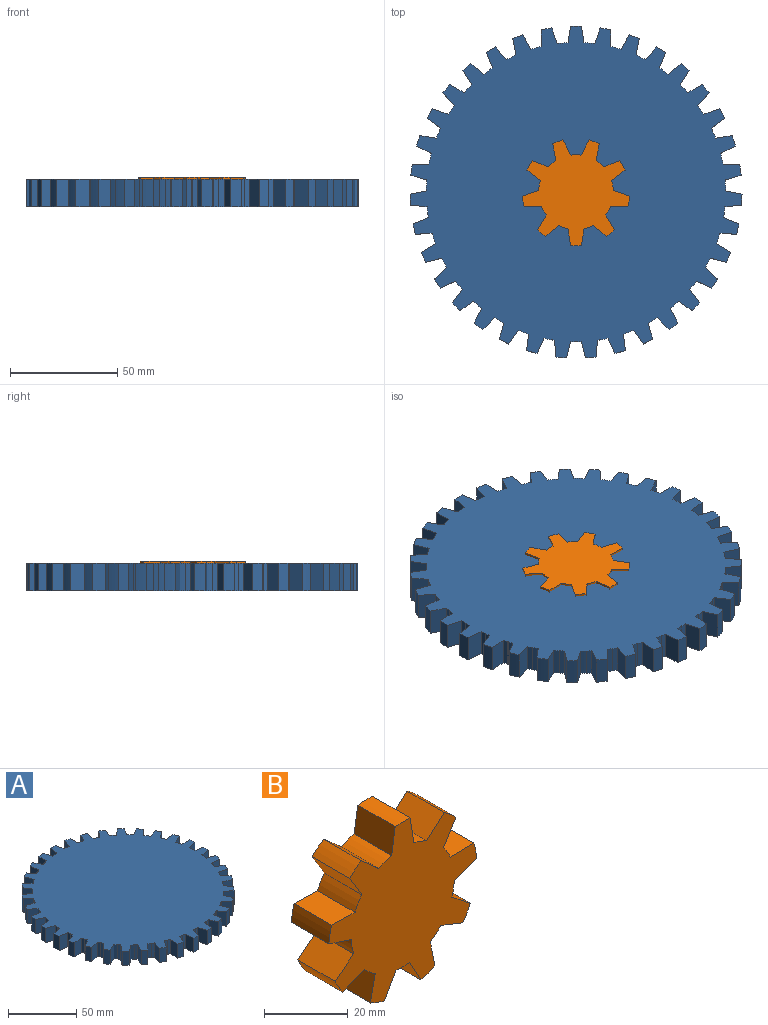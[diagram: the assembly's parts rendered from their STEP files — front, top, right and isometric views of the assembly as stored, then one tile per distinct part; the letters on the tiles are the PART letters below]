
ASSEMBLY  parts=2 mates=2
PART A: 212 faces, bbox 154.9x154.8x12.7 mm
  f0: plane 12.7x7.68mm, normal (0.99,0.15,0), area 98.7mm2, adj f1,f209,f210,f211
  f1: cylinder r=77.47mm len=12.7mm, axis (0,0,-1), area 64.5mm2, adj f0,f2,f210,f211
  f2: plane 12.7x7.68mm, normal (-0.99,0.15,0), area 98.7mm2, adj f1,f3,f210,f211
  f3: cylinder r=69.85mm len=12.7mm, axis (0,0,-1), area 32.2mm2, adj f2,f4,f210,f211
  f4: plane 12.7x0mm, normal (-0.09,1,0), area 0mm2, adj f3,f5,f210,f211
  f5: cylinder r=69.85mm len=12.7mm, axis (0,0,-1), area 32.2mm2, adj f4,f6,f210,f211
  f6: plane 12.7x7.34mm, normal (0.94,0.33,0), area 98.7mm2, adj f5,f7,f210,f211
  f7: cylinder r=77.47mm len=12.7mm, axis (0,0,-1), area 64.5mm2, adj f6,f8,f210,f211
  f8: plane 12.7x7.77mm, normal (-1,-0.03,0), area 98.7mm2, adj f7,f9,f210,f211
  f9: cylinder r=69.85mm len=12.7mm, axis (0,0,-1), area 32.2mm2, adj f8,f10,f210,f211
  f10: plane 12.7x0mm, normal (-0.27,0.96,0), area 0mm2, adj f9,f11,f210,f211
  f11: cylinder r=69.85mm len=12.7mm, axis (0,0,-1), area 32.2mm2, adj f10,f12,f210,f211
  f12: plane 12.7x6.77mm, normal (0.87,0.49,0), area 98.7mm2, adj f11,f13,f210,f211
  f13: cylinder r=77.47mm len=12.7mm, axis (0,0,-1), area 64.5mm2, adj f12,f14,f210,f211
  f14: plane 12.7x7.61mm, normal (-0.98,-0.2,0), area 98.7mm2, adj f13,f15,f210,f211
  f15: cylinder r=69.85mm len=12.7mm, axis (0,0,-1), area 32.2mm2, adj f14,f16,f210,f211
  f16: plane 12.7x0mm, normal (-0.43,0.9,0), area 0mm2, adj f15,f17,f210,f211
  f17: cylinder r=69.85mm len=12.7mm, axis (0,0,-1), area 32.2mm2, adj f16,f18,f210,f211
  f18: plane 12.7x5.98mm, normal (0.77,0.64,0), area 98.7mm2, adj f17,f19,f210,f211
  f19: cylinder r=77.47mm len=12.7mm, axis (0,0,-1), area 64.5mm2, adj f18,f20,f210,f211
  f20: plane 12.7x7.2mm, normal (-0.93,-0.38,0), area 98.7mm2, adj f19,f21,f210,f211
  f21: cylinder r=69.85mm len=12.7mm, axis (0,0,-1), area 32.2mm2, adj f20,f22,f210,f211
  f22: plane 12.7x0mm, normal (-0.59,0.81,0), area 0mm2, adj f21,f23,f210,f211
  f23: cylinder r=69.85mm len=12.7mm, axis (0,0,-1), area 32.2mm2, adj f22,f24,f210,f211
  f24: plane 12.7x5.95mm, normal (0.64,0.77,0), area 98.7mm2, adj f23,f25,f210,f211
  f25: cylinder r=77.47mm len=12.7mm, axis (0,0,-1), area 64.5mm2, adj f24,f26,f210,f211
  f26: plane 12.7x6.57mm, normal (-0.84,-0.53,0), area 98.7mm2, adj f25,f27,f210,f211
  f27: cylinder r=69.85mm len=12.7mm, axis (0,0,-1), area 32.2mm2, adj f26,f28,f210,f211
  f28: plane 12.7x0mm, normal (-0.72,0.69,0), area 0mm2, adj f27,f29,f210,f211
  f29: cylinder r=69.85mm len=12.7mm, axis (0,0,-1), area 32.2mm2, adj f28,f30,f210,f211
  f30: plane 12.7x6.75mm, normal (0.5,0.87,0), area 98.7mm2, adj f29,f31,f210,f211
  f31: cylinder r=77.47mm len=12.7mm, axis (0,0,-1), area 64.5mm2, adj f30,f32,f210,f211
  f32: plane 12.7x5.72mm, normal (-0.74,-0.68,0), area 98.7mm2, adj f31,f33,f210,f211
  f33: cylinder r=69.85mm len=12.7mm, axis (0,0,-1), area 32.2mm2, adj f32,f34,f210,f211
  f34: plane 12.7x0mm, normal (-0.83,0.55,0), area 0mm2, adj f33,f35,f210,f211
  f35: cylinder r=69.85mm len=12.7mm, axis (0,0,-1), area 32.2mm2, adj f34,f36,f210,f211
  f36: plane 12.7x7.33mm, normal (0.33,0.94,0), area 98.7mm2, adj f35,f37,f210,f211
  f37: cylinder r=77.47mm len=12.7mm, axis (0,0,-1), area 64.5mm2, adj f36,f38,f210,f211
  f38: plane 12.7x6.2mm, normal (-0.6,-0.8,0), area 98.7mm2, adj f37,f39,f210,f211
  f39: cylinder r=69.85mm len=12.7mm, axis (0,0,-1), area 32.2mm2, adj f38,f40,f210,f211
  f40: plane 12.7x0mm, normal (-0.92,0.39,0), area 0mm2, adj f39,f41,f210,f211
  f41: cylinder r=69.85mm len=12.7mm, axis (0,0,-1), area 32.2mm2, adj f40,f42,f210,f211
  f42: plane 12.7x7.67mm, normal (0.16,0.99,0), area 98.7mm2, adj f41,f43,f210,f211
  f43: cylinder r=77.47mm len=12.7mm, axis (0,0,-1), area 64.5mm2, adj f42,f44,f210,f211
  f44: plane 12.7x6.93mm, normal (-0.45,-0.89,0), area 98.7mm2, adj f43,f45,f210,f211
  f45: cylinder r=69.85mm len=12.7mm, axis (0,0,-1), area 32.2mm2, adj f44,f46,f210,f211
  f46: plane 12.7x0mm, normal (-0.97,0.22,0), area 0mm2, adj f45,f47,f210,f211
  f47: cylinder r=69.85mm len=12.7mm, axis (0,0,-1), area 32.2mm2, adj f46,f48,f210,f211
  f48: plane 12.7x7.77mm, normal (-0.02,1,0), area 98.7mm2, adj f47,f49,f210,f211
  f49: cylinder r=77.47mm len=12.7mm, axis (0,0,-1), area 64.5mm2, adj f48,f50,f210,f211
  f50: plane 12.7x7.45mm, normal (-0.28,-0.96,0), area 98.7mm2, adj f49,f51,f210,f211
  f51: cylinder r=69.85mm len=12.7mm, axis (0,0,-1), area 32.2mm2, adj f50,f52,f210,f211
  f52: plane 12.7x0mm, normal (-1,0.04,0), area 0mm2, adj f51,f53,f210,f211
  f53: cylinder r=69.85mm len=12.7mm, axis (0,0,-1), area 32.2mm2, adj f52,f54,f210,f211
  f54: plane 12.7x7.62mm, normal (-0.2,0.98,0), area 98.7mm2, adj f53,f55,f210,f211
  f55: cylinder r=77.47mm len=12.7mm, axis (0,0,-1), area 64.5mm2, adj f54,f56,f210,f211
  f56: plane 12.7x7.72mm, normal (-0.11,-0.99,0), area 98.7mm2, adj f55,f57,f210,f211
  f57: cylinder r=69.85mm len=12.7mm, axis (0,0,-1), area 32.2mm2, adj f56,f58,f210,f211
  f58: plane 12.7x0mm, normal (-0.99,-0.13,0), area 0mm2, adj f57,f59,f210,f211
  f59: cylinder r=69.85mm len=12.7mm, axis (0,0,-1), area 32.2mm2, adj f58,f60,f210,f211
  f60: plane 12.7x7.22mm, normal (-0.37,0.93,0), area 98.7mm2, adj f59,f61,f210,f211
  f61: cylinder r=77.47mm len=12.7mm, axis (0,0,-1), area 64.5mm2, adj f60,f62,f210,f211
  f62: plane 12.7x7.75mm, normal (0.07,-1,0), area 98.7mm2, adj f61,f63,f210,f211
  f63: cylinder r=69.85mm len=12.7mm, axis (0,0,-1), area 32.2mm2, adj f62,f64,f210,f211
  f64: plane 12.7x0mm, normal (-0.95,-0.31,0), area 0mm2, adj f63,f65,f210,f211
  f65: cylinder r=69.85mm len=12.7mm, axis (0,0,-1), area 32.2mm2, adj f64,f66,f210,f211
  f66: plane 12.7x6.59mm, normal (-0.53,0.85,0), area 98.7mm2, adj f65,f67,f210,f211
  f67: cylinder r=77.47mm len=12.7mm, axis (0,0,-1), area 64.5mm2, adj f66,f68,f210,f211
  f68: plane 12.7x7.53mm, normal (0.25,-0.97,0), area 98.7mm2, adj f67,f69,f210,f211
  f69: cylinder r=69.85mm len=12.7mm, axis (0,0,-1), area 32.2mm2, adj f68,f70,f210,f211
  f70: plane 12.7x0mm, normal (-0.88,-0.47,0), area 0mm2, adj f69,f71,f210,f211
  f71: cylinder r=69.85mm len=12.7mm, axis (0,0,-1), area 32.2mm2, adj f70,f72,f210,f211
  f72: plane 12.7x5.75mm, normal (-0.67,0.74,0), area 98.7mm2, adj f71,f73,f210,f211
  f73: cylinder r=77.47mm len=12.7mm, axis (0,0,-1), area 64.5mm2, adj f72,f74,f210,f211
  f74: plane 12.7x7.06mm, normal (0.42,-0.91,0), area 98.7mm2, adj f73,f75,f210,f211
  f75: cylinder r=69.85mm len=12.7mm, axis (0,0,-1), area 32.2mm2, adj f74,f76,f210,f211
  f76: plane 12.7x0mm, normal (-0.78,-0.62,0), area 0mm2, adj f75,f77,f210,f211
  f77: cylinder r=69.85mm len=12.7mm, axis (0,0,-1), area 32.2mm2, adj f76,f78,f210,f211
  f78: plane 12.7x6.17mm, normal (-0.79,0.61,0), area 98.7mm2, adj f77,f79,f210,f211
  f79: cylinder r=77.47mm len=12.7mm, axis (0,0,-1), area 64.5mm2, adj f78,f80,f210,f211
  f80: plane 12.7x6.37mm, normal (0.57,-0.82,0), area 98.7mm2, adj f79,f81,f210,f211
  f81: cylinder r=69.85mm len=12.7mm, axis (0,0,-1), area 32.2mm2, adj f80,f82,f210,f211
  f82: plane 12.7x0mm, normal (-0.66,-0.75,0), area 0mm2, adj f81,f83,f210,f211
  f83: cylinder r=69.85mm len=12.7mm, axis (0,0,-1), area 32.2mm2, adj f82,f84,f210,f211
  f84: plane 12.7x6.91mm, normal (-0.89,0.46,0), area 98.7mm2, adj f83,f85,f210,f211
  f85: cylinder r=77.47mm len=12.7mm, axis (0,0,-1), area 64.5mm2, adj f84,f86,f210,f211
  f86: plane 12.7x5.51mm, normal (0.71,-0.7,0), area 98.7mm2, adj f85,f87,f210,f211
  f87: cylinder r=69.85mm len=12.7mm, axis (0,0,-1), area 32.2mm2, adj f86,f88,f210,f211
  f88: plane 12.7x0mm, normal (-0.51,-0.86,0), area 0mm2, adj f87,f89,f210,f211
  f89: cylinder r=69.85mm len=12.7mm, axis (0,0,-1), area 32.2mm2, adj f88,f90,f210,f211
  f90: plane 12.7x7.43mm, normal (-0.96,0.29,0), area 98.7mm2, adj f89,f91,f210,f211
  f91: cylinder r=77.47mm len=12.7mm, axis (0,0,-1), area 64.5mm2, adj f90,f92,f210,f211
  f92: plane 12.7x6.4mm, normal (0.82,-0.57,0), area 98.7mm2, adj f91,f93,f210,f211
  f93: cylinder r=69.85mm len=12.7mm, axis (0,0,-1), area 32.2mm2, adj f92,f94,f210,f211
  f94: plane 12.7x0mm, normal (-0.35,-0.94,0), area 0mm2, adj f93,f95,f210,f211
  f95: cylinder r=69.85mm len=12.7mm, axis (0,0,-1), area 32.2mm2, adj f94,f96,f210,f211
  f96: plane 12.7x7.72mm, normal (-0.99,0.12,0), area 98.7mm2, adj f95,f97,f210,f211
  f97: cylinder r=77.47mm len=12.7mm, axis (0,0,-1), area 64.5mm2, adj f96,f98,f210,f211
  f98: plane 12.7x7.08mm, normal (0.91,-0.41,0), area 98.7mm2, adj f97,f99,f210,f211
  f99: cylinder r=69.85mm len=12.7mm, axis (0,0,-1), area 32.2mm2, adj f98,f100,f210,f211
  f100: plane 12.7x0mm, normal (-0.18,-0.98,0), area 0mm2, adj f99,f101,f210,f211
  f101: cylinder r=69.85mm len=12.7mm, axis (0,0,-1), area 32.2mm2, adj f100,f102,f210,f211
  f102: plane 12.7x7.75mm, normal (-1,-0.06,0), area 98.7mm2, adj f101,f103,f210,f211
  f103: cylinder r=77.47mm len=12.7mm, axis (0,0,-1), area 64.5mm2, adj f102,f104,f210,f211
  f104: plane 12.7x7.54mm, normal (0.97,-0.24,0), area 98.7mm2, adj f103,f105,f210,f211
  f105: cylinder r=69.85mm len=12.7mm, axis (0,0,-1), area 32.2mm2, adj f104,f106,f210,f211
  f106: plane 12.7x0mm, normal (0,-1,0), area 0mm2, adj f105,f107,f210,f211
  f107: cylinder r=69.85mm len=12.7mm, axis (0,0,-1), area 32.2mm2, adj f106,f108,f210,f211
  f108: plane 12.7x7.54mm, normal (-0.97,-0.24,0), area 98.7mm2, adj f107,f109,f210,f211
  f109: cylinder r=77.47mm len=12.7mm, axis (0,0,-1), area 64.5mm2, adj f108,f110,f210,f211
  f110: plane 12.7x7.75mm, normal (1,-0.06,0), area 98.7mm2, adj f109,f111,f210,f211
  f111: cylinder r=69.85mm len=12.7mm, axis (0,0,-1), area 32.2mm2, adj f110,f112,f210,f211
  f112: plane 12.7x0mm, normal (0.18,-0.98,0), area 0mm2, adj f111,f113,f210,f211
  f113: cylinder r=69.85mm len=12.7mm, axis (0,0,-1), area 32.2mm2, adj f112,f114,f210,f211
  f114: plane 12.7x7.08mm, normal (-0.91,-0.41,0), area 98.7mm2, adj f113,f115,f210,f211
  f115: cylinder r=77.47mm len=12.7mm, axis (0,0,-1), area 64.5mm2, adj f114,f116,f210,f211
  f116: plane 12.7x7.72mm, normal (0.99,0.12,0), area 98.7mm2, adj f115,f117,f210,f211
  f117: cylinder r=69.85mm len=12.7mm, axis (0,0,-1), area 32.2mm2, adj f116,f118,f210,f211
  f118: plane 12.7x0mm, normal (0.35,-0.94,0), area 0mm2, adj f117,f119,f210,f211
  f119: cylinder r=69.85mm len=12.7mm, axis (0,0,-1), area 32.2mm2, adj f118,f120,f210,f211
  f120: plane 12.7x6.4mm, normal (-0.82,-0.57,0), area 98.7mm2, adj f119,f121,f210,f211
  f121: cylinder r=77.47mm len=12.7mm, axis (0,0,-1), area 64.5mm2, adj f120,f122,f210,f211
  f122: plane 12.7x7.43mm, normal (0.96,0.29,0), area 98.7mm2, adj f121,f123,f210,f211
  f123: cylinder r=69.85mm len=12.7mm, axis (0,0,-1), area 32.2mm2, adj f122,f124,f210,f211
  f124: plane 12.7x0mm, normal (0.51,-0.86,0), area 0mm2, adj f123,f125,f210,f211
  f125: cylinder r=69.85mm len=12.7mm, axis (0,0,-1), area 32.2mm2, adj f124,f126,f210,f211
  f126: plane 12.7x5.51mm, normal (-0.71,-0.7,0), area 98.7mm2, adj f125,f127,f210,f211
  f127: cylinder r=77.47mm len=12.7mm, axis (0,0,-1), area 64.5mm2, adj f126,f128,f210,f211
  f128: plane 12.7x6.91mm, normal (0.89,0.46,0), area 98.7mm2, adj f127,f129,f210,f211
  f129: cylinder r=69.85mm len=12.7mm, axis (0,0,-1), area 32.2mm2, adj f128,f130,f210,f211
  f130: plane 12.7x0mm, normal (0.66,-0.75,0), area 0mm2, adj f129,f131,f210,f211
  f131: cylinder r=69.85mm len=12.7mm, axis (0,0,-1), area 32.2mm2, adj f130,f132,f210,f211
  f132: plane 12.7x6.37mm, normal (-0.57,-0.82,0), area 98.7mm2, adj f131,f133,f210,f211
  f133: cylinder r=77.47mm len=12.7mm, axis (0,0,-1), area 64.5mm2, adj f132,f134,f210,f211
  f134: plane 12.7x6.17mm, normal (0.79,0.61,0), area 98.7mm2, adj f133,f135,f210,f211
  f135: cylinder r=69.85mm len=12.7mm, axis (0,0,-1), area 32.2mm2, adj f134,f136,f210,f211
  f136: plane 12.7x0mm, normal (0.78,-0.62,0), area 0mm2, adj f135,f137,f210,f211
  f137: cylinder r=69.85mm len=12.7mm, axis (0,0,-1), area 32.2mm2, adj f136,f138,f210,f211
  f138: plane 12.7x7.06mm, normal (-0.42,-0.91,0), area 98.7mm2, adj f137,f139,f210,f211
  f139: cylinder r=77.47mm len=12.7mm, axis (0,0,-1), area 64.5mm2, adj f138,f140,f210,f211
  f140: plane 12.7x5.75mm, normal (0.67,0.74,0), area 98.7mm2, adj f139,f141,f210,f211
  f141: cylinder r=69.85mm len=12.7mm, axis (0,0,-1), area 32.2mm2, adj f140,f142,f210,f211
  f142: plane 12.7x0mm, normal (0.88,-0.47,0), area 0mm2, adj f141,f143,f210,f211
  f143: cylinder r=69.85mm len=12.7mm, axis (0,0,-1), area 32.2mm2, adj f142,f144,f210,f211
  f144: plane 12.7x7.53mm, normal (-0.25,-0.97,0), area 98.7mm2, adj f143,f145,f210,f211
  f145: cylinder r=77.47mm len=12.7mm, axis (0,0,-1), area 64.5mm2, adj f144,f146,f210,f211
  f146: plane 12.7x6.59mm, normal (0.53,0.85,0), area 98.7mm2, adj f145,f147,f210,f211
  f147: cylinder r=69.85mm len=12.7mm, axis (0,0,-1), area 32.2mm2, adj f146,f148,f210,f211
  f148: plane 12.7x0mm, normal (0.95,-0.31,0), area 0mm2, adj f147,f149,f210,f211
  f149: cylinder r=69.85mm len=12.7mm, axis (0,0,-1), area 32.2mm2, adj f148,f150,f210,f211
  f150: plane 12.7x7.75mm, normal (-0.07,-1,0), area 98.7mm2, adj f149,f151,f210,f211
  f151: cylinder r=77.47mm len=12.7mm, axis (0,0,-1), area 64.5mm2, adj f150,f152,f210,f211
  f152: plane 12.7x7.22mm, normal (0.37,0.93,0), area 98.7mm2, adj f151,f153,f210,f211
  f153: cylinder r=69.85mm len=12.7mm, axis (0,0,-1), area 32.2mm2, adj f152,f154,f210,f211
  f154: plane 12.7x0mm, normal (0.99,-0.13,0), area 0mm2, adj f153,f155,f210,f211
  f155: cylinder r=69.85mm len=12.7mm, axis (0,0,-1), area 32.2mm2, adj f154,f156,f210,f211
  f156: plane 12.7x7.72mm, normal (0.11,-0.99,0), area 98.7mm2, adj f155,f157,f210,f211
  f157: cylinder r=77.47mm len=12.7mm, axis (0,0,-1), area 64.5mm2, adj f156,f158,f210,f211
  f158: plane 12.7x7.62mm, normal (0.2,0.98,0), area 98.7mm2, adj f157,f159,f210,f211
  f159: cylinder r=69.85mm len=12.7mm, axis (0,0,-1), area 32.2mm2, adj f158,f160,f210,f211
  f160: plane 12.7x0mm, normal (1,0.04,0), area 0mm2, adj f159,f161,f210,f211
  f161: cylinder r=69.85mm len=12.7mm, axis (0,0,-1), area 32.2mm2, adj f160,f162,f210,f211
  f162: plane 12.7x7.45mm, normal (0.28,-0.96,0), area 98.7mm2, adj f161,f163,f210,f211
  f163: cylinder r=77.47mm len=12.7mm, axis (0,0,-1), area 64.5mm2, adj f162,f164,f210,f211
  f164: plane 12.7x7.77mm, normal (0.02,1,0), area 98.7mm2, adj f163,f165,f210,f211
  f165: cylinder r=69.85mm len=12.7mm, axis (0,0,-1), area 32.2mm2, adj f164,f166,f210,f211
  f166: plane 12.7x0mm, normal (0.97,0.22,0), area 0mm2, adj f165,f167,f210,f211
  f167: cylinder r=69.85mm len=12.7mm, axis (0,0,-1), area 32.2mm2, adj f166,f168,f210,f211
  f168: plane 12.7x6.93mm, normal (0.45,-0.89,0), area 98.7mm2, adj f167,f169,f210,f211
  f169: cylinder r=77.47mm len=12.7mm, axis (0,0,-1), area 64.5mm2, adj f168,f170,f210,f211
  f170: plane 12.7x7.67mm, normal (-0.16,0.99,0), area 98.7mm2, adj f169,f171,f210,f211
  f171: cylinder r=69.85mm len=12.7mm, axis (0,0,-1), area 32.2mm2, adj f170,f172,f210,f211
  f172: plane 12.7x0mm, normal (0.92,0.39,0), area 0mm2, adj f171,f173,f210,f211
  f173: cylinder r=69.85mm len=12.7mm, axis (0,0,-1), area 32.2mm2, adj f172,f174,f210,f211
  f174: plane 12.7x6.2mm, normal (0.6,-0.8,0), area 98.7mm2, adj f173,f175,f210,f211
  f175: cylinder r=77.47mm len=12.7mm, axis (0,0,-1), area 64.5mm2, adj f174,f176,f210,f211
  f176: plane 12.7x7.33mm, normal (-0.33,0.94,0), area 98.7mm2, adj f175,f177,f210,f211
  f177: cylinder r=69.85mm len=12.7mm, axis (0,0,-1), area 32.2mm2, adj f176,f178,f210,f211
  f178: plane 12.7x0mm, normal (0.83,0.55,0), area 0mm2, adj f177,f179,f210,f211
  f179: cylinder r=69.85mm len=12.7mm, axis (0,0,-1), area 32.2mm2, adj f178,f180,f210,f211
  f180: plane 12.7x5.72mm, normal (0.74,-0.68,0), area 98.7mm2, adj f179,f181,f210,f211
  f181: cylinder r=77.47mm len=12.7mm, axis (0,0,-1), area 64.5mm2, adj f180,f182,f210,f211
  f182: plane 12.7x6.75mm, normal (-0.5,0.87,0), area 98.7mm2, adj f181,f183,f210,f211
  f183: cylinder r=69.85mm len=12.7mm, axis (0,0,-1), area 32.2mm2, adj f182,f184,f210,f211
  f184: plane 12.7x0mm, normal (0.72,0.69,0), area 0mm2, adj f183,f185,f210,f211
  f185: cylinder r=69.85mm len=12.7mm, axis (0,0,-1), area 32.2mm2, adj f184,f186,f210,f211
  f186: plane 12.7x6.57mm, normal (0.84,-0.53,0), area 98.7mm2, adj f185,f187,f210,f211
  f187: cylinder r=77.47mm len=12.7mm, axis (0,0,-1), area 64.5mm2, adj f186,f188,f210,f211
  f188: plane 12.7x5.95mm, normal (-0.64,0.77,0), area 98.7mm2, adj f187,f189,f210,f211
  f189: cylinder r=69.85mm len=12.7mm, axis (0,0,-1), area 32.2mm2, adj f188,f190,f210,f211
  f190: plane 12.7x0mm, normal (0.59,0.81,0), area 0mm2, adj f189,f191,f210,f211
  f191: cylinder r=69.85mm len=12.7mm, axis (0,0,-1), area 32.2mm2, adj f190,f192,f210,f211
  f192: plane 12.7x7.2mm, normal (0.93,-0.38,0), area 98.7mm2, adj f191,f193,f210,f211
  f193: cylinder r=77.47mm len=12.7mm, axis (0,0,-1), area 64.5mm2, adj f192,f194,f210,f211
  f194: plane 12.7x5.98mm, normal (-0.77,0.64,0), area 98.7mm2, adj f193,f195,f210,f211
  f195: cylinder r=69.85mm len=12.7mm, axis (0,0,-1), area 32.2mm2, adj f194,f196,f210,f211
  f196: plane 12.7x0mm, normal (0.43,0.9,0), area 0mm2, adj f195,f197,f210,f211
  f197: cylinder r=69.85mm len=12.7mm, axis (0,0,-1), area 32.2mm2, adj f196,f198,f210,f211
  f198: plane 12.7x7.61mm, normal (0.98,-0.2,0), area 98.7mm2, adj f197,f199,f210,f211
  f199: cylinder r=77.47mm len=12.7mm, axis (0,0,-1), area 64.5mm2, adj f198,f200,f210,f211
  f200: plane 12.7x6.77mm, normal (-0.87,0.49,0), area 98.7mm2, adj f199,f201,f210,f211
  f201: cylinder r=69.85mm len=12.7mm, axis (0,0,-1), area 32.2mm2, adj f200,f202,f210,f211
  f202: plane 12.7x0mm, normal (0.27,0.96,0), area 0mm2, adj f201,f203,f210,f211
  f203: cylinder r=69.85mm len=12.7mm, axis (0,0,-1), area 32.2mm2, adj f202,f204,f210,f211
  f204: plane 12.7x7.77mm, normal (1,-0.03,0), area 98.7mm2, adj f203,f205,f210,f211
  f205: cylinder r=77.47mm len=12.7mm, axis (0,0,-1), area 64.5mm2, adj f204,f206,f210,f211
  f206: plane 12.7x7.34mm, normal (-0.94,0.33,0), area 98.7mm2, adj f205,f207,f210,f211
  f207: cylinder r=69.85mm len=12.7mm, axis (0,0,-1), area 32.2mm2, adj f206,f208,f210,f211
  f208: plane 12.7x0mm, normal (0.09,1,0), area 0mm2, adj f207,f209,f210,f211
  f209: cylinder r=69.85mm len=12.7mm, axis (0,0,-1), area 32.2mm2, adj f0,f208,f210,f211
  f210: plane 154.93x154.81mm, normal (0,0,1), area 17000.4mm2, adj f0,f1,f2,f3,f4,f5,f6,f7
  f211: plane 154.93x154.81mm, normal (0,0,-1), area 17000.4mm2, adj f0,f1,f2,f3,f4,f5,f6,f7
PART B: 38 faces, bbox 50x12.7x49.4 mm
  f0: plane 12.7x7.83mm, normal (0.98,0,0.2), area 101.4mm2, adj f1,f35,f36,f37
  f1: cylinder r=17.46mm len=12.7mm, axis (0,1,0), area 59.3mm2, adj f0,f2,f36,f37
  f2: plane 12.7x7.43mm, normal (-0.36,0,-0.93), area 101.4mm2, adj f1,f3,f36,f37
  f3: cylinder r=25.08mm len=12.7mm, axis (0,1,0), area 64.6mm2, adj f2,f4,f36,f37
  f4: plane 12.7x6.24mm, normal (0.62,0,0.78), area 101.4mm2, adj f3,f5,f36,f37
  f5: cylinder r=17.46mm len=12.7mm, axis (0,1,0), area 59.3mm2, adj f4,f6,f36,f37
  f6: plane 12.7x7.57mm, normal (0.32,0,-0.95), area 101.4mm2, adj f5,f7,f36,f37
  f7: cylinder r=25.08mm len=12.7mm, axis (0,1,0), area 64.6mm2, adj f6,f8,f36,f37
  f8: plane 12.7x7.98mm, normal (-0.02,0,1), area 101.4mm2, adj f7,f9,f36,f37
  f9: cylinder r=17.46mm len=12.7mm, axis (0,1,0), area 59.3mm2, adj f8,f10,f36,f37
  f10: plane 12.7x6.82mm, normal (0.85,0,-0.52), area 101.4mm2, adj f9,f11,f36,f37
  f11: cylinder r=25.08mm len=12.7mm, axis (0,1,0), area 64.6mm2, adj f10,f12,f36,f37
  f12: plane 12.7x5.99mm, normal (-0.66,0,0.75), area 101.4mm2, adj f11,f13,f36,f37
  f13: cylinder r=17.46mm len=12.7mm, axis (0,1,0), area 59.3mm2, adj f12,f14,f36,f37
  f14: plane 12.7x7.9mm, normal (0.99,0,0.15), area 101.4mm2, adj f13,f15,f36,f37
  f15: cylinder r=25.08mm len=12.7mm, axis (0,1,0), area 64.6mm2, adj f14,f16,f36,f37
  f16: plane 12.7x7.9mm, normal (-0.99,0,0.15), area 101.4mm2, adj f15,f17,f36,f37
  f17: cylinder r=17.46mm len=12.7mm, axis (0,1,0), area 59.3mm2, adj f16,f18,f36,f37
  f18: plane 12.7x5.99mm, normal (0.66,0,0.75), area 101.4mm2, adj f17,f19,f36,f37
  f19: cylinder r=25.08mm len=12.7mm, axis (0,1,0), area 64.6mm2, adj f18,f20,f36,f37
  f20: plane 12.7x6.82mm, normal (-0.85,0,-0.52), area 101.4mm2, adj f19,f21,f36,f37
  f21: cylinder r=17.46mm len=12.7mm, axis (0,1,0), area 59.3mm2, adj f20,f22,f36,f37
  f22: plane 12.7x7.98mm, normal (0.02,0,1), area 101.4mm2, adj f21,f23,f36,f37
  f23: cylinder r=25.08mm len=12.7mm, axis (0,1,0), area 64.6mm2, adj f22,f24,f36,f37
  f24: plane 12.7x7.57mm, normal (-0.32,0,-0.95), area 101.4mm2, adj f23,f25,f36,f37
  f25: cylinder r=17.46mm len=12.7mm, axis (0,1,0), area 59.3mm2, adj f24,f26,f36,f37
  f26: plane 12.7x6.24mm, normal (-0.62,0,0.78), area 101.4mm2, adj f25,f27,f36,f37
  f27: cylinder r=25.08mm len=12.7mm, axis (0,1,0), area 64.6mm2, adj f26,f28,f36,f37
  f28: plane 12.7x7.43mm, normal (0.36,0,-0.93), area 101.4mm2, adj f27,f29,f36,f37
  f29: cylinder r=17.46mm len=12.7mm, axis (0,1,0), area 59.3mm2, adj f28,f30,f36,f37
  f30: plane 12.7x7.83mm, normal (-0.98,0,0.2), area 101.4mm2, adj f29,f31,f36,f37
  f31: cylinder r=25.08mm len=12.7mm, axis (0,1,0), area 64.6mm2, adj f30,f32,f36,f37
  f32: plane 12.7x7.01mm, normal (0.88,0,-0.48), area 101.4mm2, adj f31,f33,f36,f37
  f33: cylinder r=17.46mm len=12.7mm, axis (0,1,0), area 59.3mm2, adj f32,f34,f36,f37
  f34: plane 12.7x7.01mm, normal (-0.88,0,-0.48), area 101.4mm2, adj f33,f35,f36,f37
  f35: cylinder r=25.08mm len=12.7mm, axis (0,1,0), area 64.6mm2, adj f0,f34,f36,f37
  f36: plane 50.03x49.4mm, normal (0,-1,0), area 1389.6mm2, adj f0,f1,f2,f3,f4,f5,f6,f7
  f37: plane 50.03x49.4mm, normal (0,1,0), area 1389.6mm2, adj f0,f1,f2,f3,f4,f5,f6,f7
PLACE A t=(73.22,-92.28,6.21)mm
PLACE B rot(axis=(1,0,0),90deg) t=(73.22,-92.28,19.87)mm
MATE cylindrical B.f35 <-> A.f1  axis (0,0,-1) through (73.22,-92.28,7.17)mm
MATE parallel B.f1 <-> A.f13  axis (0,0,1) through (73.22,-92.28,19.87)mm
